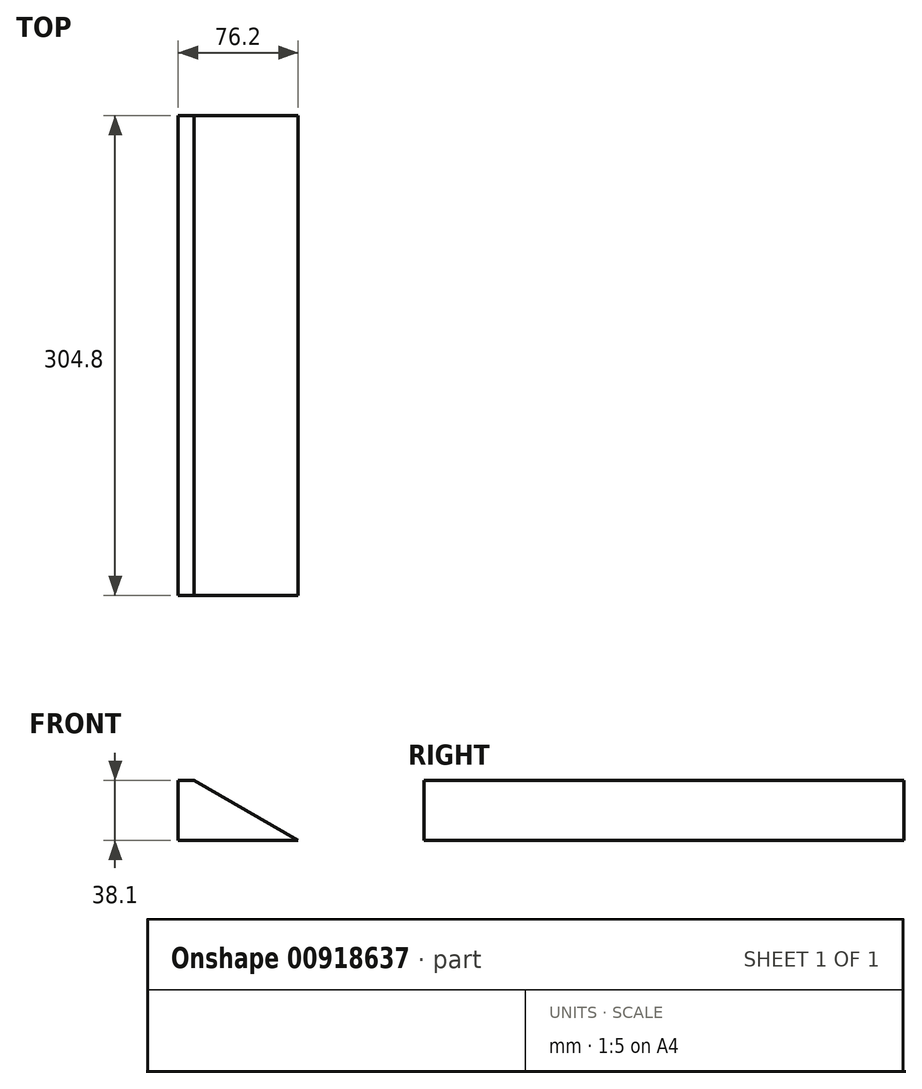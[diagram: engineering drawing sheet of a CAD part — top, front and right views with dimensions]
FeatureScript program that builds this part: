
annotation { "Feature Type Name" : "Feature", "Feature Type Description" : "" }
export const myFeature = defineFeature(function(context is Context, id is Id, definition is map)
    precondition{}
    {
        {
            var Q0;
            Q0=qCreatedBy(makeId("Front.planeOp"),FACE);
            var sketch = newSketch(context, id + "F0", { "sketchPlane" : qUnion([Q0])});
            skLineSegment(sketch, "E0.bottom", {"start": v(-76.2, 19.05) * mm, "end": v(76.2, 19.05) * mm});
            skLineSegment(sketch, "E0.top", {"start": v(-76.2, -19.05) * mm, "end": v(76.2, -19.05) * mm});
            skLineSegment(sketch, "E0.left", {"start": v(-76.2, 19.05) * mm, "end": v(-76.2, -19.05) * mm});
            skLineSegment(sketch, "E0.right", {"start": v(76.2, 19.05) * mm, "end": v(76.2, -19.05) * mm});
            skLineSegment(sketch, "E1", {"start": v(-76.2, 19.05) * mm, "end": v(76.2, -19.05) * mm, "construction": true});
            skSolve(sketch);
        }
        {
            var Q0;
            Q0=makeQuery(id+"F0.imprint","IMPRINT",FACE,{"disambiguationData":[TD([[makeQuery(id+"F0.imprint","IMPRINT",EDGE,{"derivedFrom":sQuery(id+"F0.wireOp",EDGE,"E0.bottom")}),-1.0]])]});
            extrude(context, id + "F1", {"entities" : qUnion([Q0]), "depth" : 304.8 * mm, "offsetDistance" : 25.4 * mm, "symmetric" : true});
        }
        {
            var Q0;
            Q0=makeQuery(id+"F1.opExtrude","CAP_FACE",FACE,{"disambiguationData":[OSD([sQuery(id+"F0.wireOp",EDGE,"E0.bottom"),sQuery(id+"F0.wireOp",EDGE,"E0.top"),sQuery(id+"F0.wireOp",EDGE,"E0.left"),sQuery(id+"F0.wireOp",EDGE,"E0.right")])],"isStart":false});
            var sketch = newSketch(context, id + "F2", { "sketchPlane" : qUnion([Q0])});
            skLineSegment(sketch, "E2", {"start": v(10.2, 19.05) * mm, "end": v(76.2, -19.05) * mm});
            skLineSegment(sketch, "E3", {"start": v(76.2, 19.05) * mm, "end": v(76.2, -19.05) * mm});
            skLineSegment(sketch, "E4", {"start": v(76.2, 19.05) * mm, "end": v(10.2, 19.05) * mm});
            skSolve(sketch);
        }
        {
            var Q0;
            Q0=makeQuery(id+"F2.imprint","IMPRINT",FACE,{"disambiguationData":[TD([[makeQuery(id+"F2.imprint","IMPRINT",EDGE,{"derivedFrom":sQuery(id+"F2.wireOp",EDGE,"E2")}),1.0]])]});
            extrude(context, id + "F3", {"entities" : qUnion([Q0]), "operationType" : NewBodyOperationType.REMOVE, "endBound" : BoundingType.THROUGH_ALL, "oppositeDirection" : true, "depth" : 25.4 * mm, "offsetDistance" : 25.4 * mm});
        }
        {
            var Q0;
            Q0=makeQuery(id+"F1.opExtrude","CAP_FACE",FACE,{"disambiguationData":[OSD([sQuery(id+"F0.wireOp",EDGE,"E0.bottom"),sQuery(id+"F0.wireOp",EDGE,"E0.top"),sQuery(id+"F0.wireOp",EDGE,"E0.left"),sQuery(id+"F0.wireOp",EDGE,"E0.right")])],"isStart":false});
            var sketch = newSketch(context, id + "F4", { "sketchPlane" : qUnion([Q0])});
            skLineSegment(sketch, "E5.bottom", {"start": v(-76.2, 19.05) * mm, "end": v(0, 19.05) * mm});
            skLineSegment(sketch, "E5.top", {"start": v(-76.2, -19.05) * mm, "end": v(0, -19.05) * mm});
            skLineSegment(sketch, "E5.left", {"start": v(-76.2, 19.05) * mm, "end": v(-76.2, -19.05) * mm});
            skLineSegment(sketch, "E5.right", {"start": v(0, 19.05) * mm, "end": v(0, -19.05) * mm});
            skSolve(sketch);
        }
        {
            var Q0;
            Q0=makeQuery(id+"F4.imprint","IMPRINT",FACE,{"disambiguationData":[TD([[makeQuery(id+"F4.imprint","IMPRINT",EDGE,{"derivedFrom":sQuery(id+"F4.wireOp",EDGE,"E5.bottom")}),-1.0]])]});
            extrude(context, id + "F5", {"entities" : qUnion([Q0]), "operationType" : NewBodyOperationType.REMOVE, "endBound" : BoundingType.THROUGH_ALL, "oppositeDirection" : true, "depth" : 25.4 * mm, "offsetDistance" : 25.4 * mm});
        }
    });
